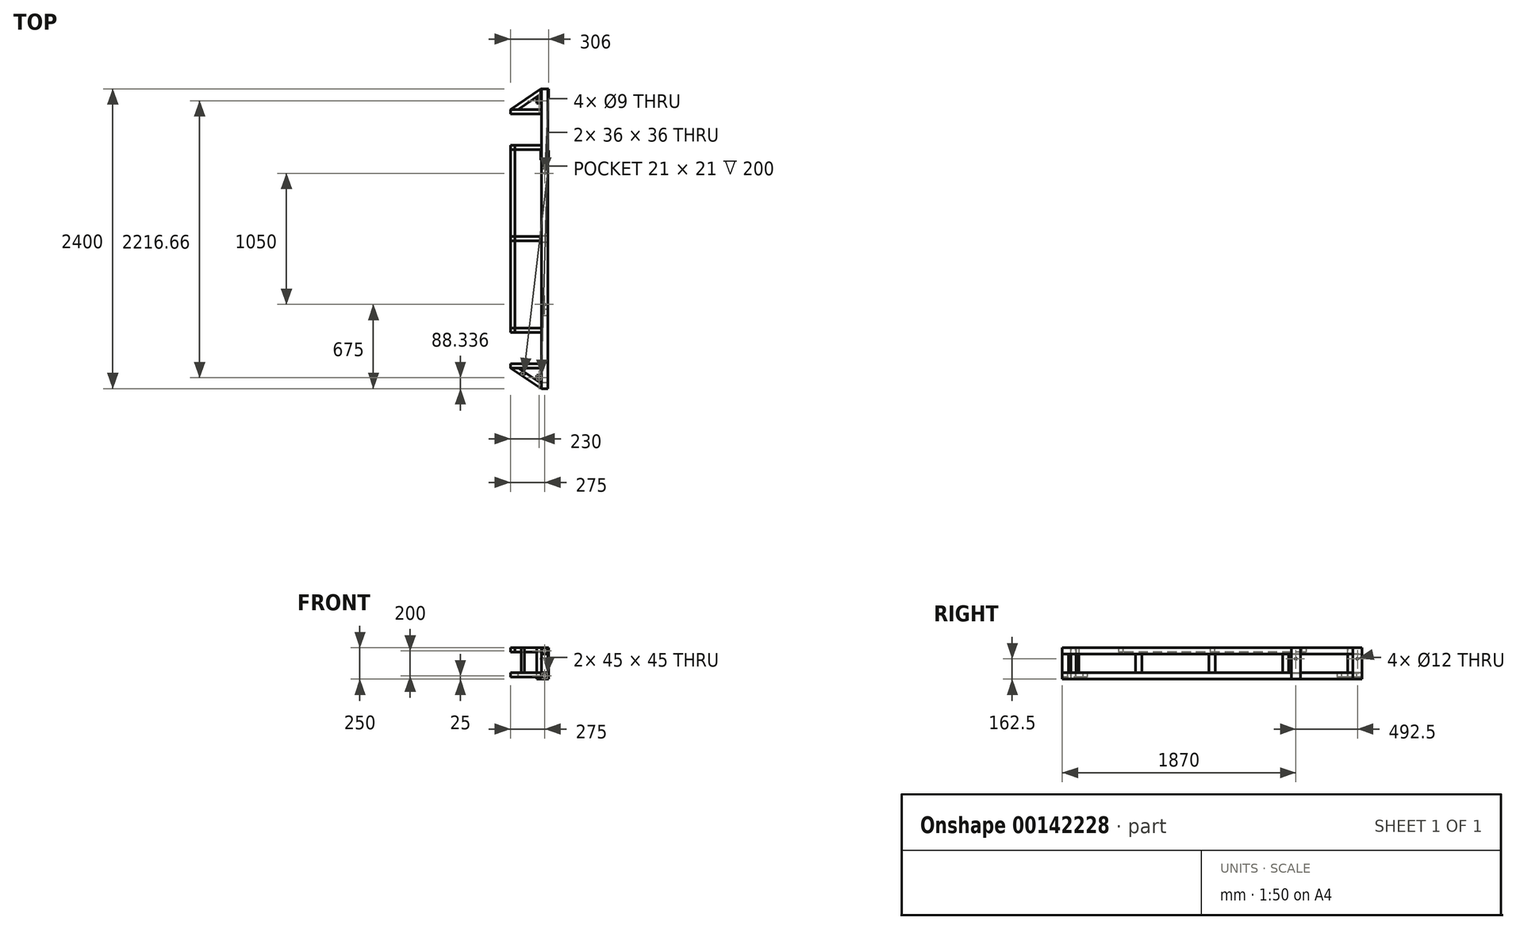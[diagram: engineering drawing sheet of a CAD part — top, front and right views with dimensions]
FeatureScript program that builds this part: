
annotation { "Feature Type Name" : "Feature", "Feature Type Description" : "" }
export const myFeature = defineFeature(function(context is Context, id is Id, definition is map)
    precondition{}
    {
        {
            var Q0;
            Q0=qCreatedBy(makeId("Front.planeOp"),FACE);
            var sketch = newSketch(context, id + "F0", { "sketchPlane" : qUnion([Q0])});
            skLineSegment(sketch, "E0.bottom", {"start": v(0, 125) * mm, "end": v(50, 125) * mm});
            skLineSegment(sketch, "E0.top", {"start": v(0, 75) * mm, "end": v(50, 75) * mm});
            skLineSegment(sketch, "E0.left", {"start": v(0, 125) * mm, "end": v(0, 75) * mm});
            skLineSegment(sketch, "E0.right", {"start": v(50, 125) * mm, "end": v(50, 75) * mm});
            skLineSegment(sketch, "E1.bottom", {"start": v(2.5, 122.5) * mm, "end": v(47.5, 122.5) * mm});
            skLineSegment(sketch, "E1.top", {"start": v(2.5, 77.5) * mm, "end": v(47.5, 77.5) * mm});
            skLineSegment(sketch, "E1.left", {"start": v(2.5, 122.5) * mm, "end": v(2.5, 77.5) * mm});
            skLineSegment(sketch, "E1.right", {"start": v(47.5, 122.5) * mm, "end": v(47.5, 77.5) * mm});
            skLineSegment(sketch, "E2.0.1.0", {"start": v(47.5, -77.5) * mm, "end": v(47.5, -122.5) * mm});
            skLineSegment(sketch, "E2.0.1.1", {"start": v(2.5, -77.5) * mm, "end": v(2.5, -122.5) * mm});
            skLineSegment(sketch, "E2.0.1.2", {"start": v(2.5, -122.5) * mm, "end": v(47.5, -122.5) * mm});
            skLineSegment(sketch, "E2.0.1.3", {"start": v(2.5, -77.5) * mm, "end": v(47.5, -77.5) * mm});
            skLineSegment(sketch, "E2.0.1.4", {"start": v(0, -75) * mm, "end": v(50, -75) * mm});
            skLineSegment(sketch, "E2.0.1.5", {"start": v(50, -75) * mm, "end": v(50, -125) * mm});
            skLineSegment(sketch, "E2.0.1.6", {"start": v(0, -75) * mm, "end": v(0, -125) * mm});
            skLineSegment(sketch, "E2.0.1.7", {"start": v(0, -125) * mm, "end": v(50, -125) * mm});
            skLineSegment(sketch, "E2.direction1", {"start": v(0, 75) * mm, "end": v(25, 75) * mm, "construction": true});
            skLineSegment(sketch, "E2.direction2", {"start": v(0, 75) * mm, "end": v(0, -125) * mm, "construction": true});
            skSolve(sketch);
        }
        {
            var Q0;
            Q0=makeQuery(id+"F0.imprint","IMPRINT",FACE,{"disambiguationData":[TD([[makeQuery(id+"F0.imprint","IMPRINT",EDGE,{"derivedFrom":sQuery(id+"F0.wireOp",EDGE,"E0.bottom")}),-1.0]])]});
            var Q1;
            Q1=makeQuery(id+"F0.imprint","IMPRINT",FACE,{"disambiguationData":[TD([[makeQuery(id+"F0.imprint","IMPRINT",EDGE,{"derivedFrom":sQuery(id+"F0.wireOp",EDGE,"E2.0.1.0")}),1.0]])]});
            extrude(context, id + "F1", {"entities" : qUnion([Q0, Q1]), "endBound" : BoundingType.SYMMETRIC, "depth" : 2400 * mm});
        }
        {
            var Q0;
            Q0=qCreatedBy(makeId("Top.planeOp"),FACE);
            var sketch = newSketch(context, id + "F2", { "sketchPlane" : qUnion([Q0])});
            skLineSegment(sketch, "E3.bottom", {"start": v(0, -1150) * mm, "end": v(50, -1150) * mm});
            skLineSegment(sketch, "E3.top", {"start": v(0, -1200) * mm, "end": v(50, -1200) * mm});
            skLineSegment(sketch, "E3.left", {"start": v(0, -1150) * mm, "end": v(0, -1200) * mm});
            skLineSegment(sketch, "E3.right", {"start": v(50, -1150) * mm, "end": v(50, -1200) * mm});
            skLineSegment(sketch, "E4.0.1.0", {"start": v(0, -562.5) * mm, "end": v(50, -562.5) * mm});
            skLineSegment(sketch, "E4.0.1.1", {"start": v(0, -612.5) * mm, "end": v(50, -612.5) * mm});
            skLineSegment(sketch, "E4.0.1.2", {"start": v(50, -562.5) * mm, "end": v(50, -612.5) * mm});
            skLineSegment(sketch, "E4.0.1.3", {"start": v(0, -562.5) * mm, "end": v(0, -612.5) * mm});
            skLineSegment(sketch, "E4.0.2.0", {"start": v(0, 25) * mm, "end": v(50, 25) * mm});
            skLineSegment(sketch, "E4.0.2.1", {"start": v(0, -25) * mm, "end": v(50, -25) * mm});
            skLineSegment(sketch, "E4.0.2.2", {"start": v(50, 25) * mm, "end": v(50, -25) * mm});
            skLineSegment(sketch, "E4.0.2.3", {"start": v(0, 25) * mm, "end": v(0, -25) * mm});
            skLineSegment(sketch, "E4.0.3.0", {"start": v(0, 612.5) * mm, "end": v(50, 612.5) * mm});
            skLineSegment(sketch, "E4.0.3.1", {"start": v(0, 562.5) * mm, "end": v(50, 562.5) * mm});
            skLineSegment(sketch, "E4.0.3.2", {"start": v(50, 612.5) * mm, "end": v(50, 562.5) * mm});
            skLineSegment(sketch, "E4.0.3.3", {"start": v(0, 612.5) * mm, "end": v(0, 562.5) * mm});
            skLineSegment(sketch, "E4.direction1", {"start": v(0, -1150) * mm, "end": v(25, -1150) * mm, "construction": true});
            skLineSegment(sketch, "E4.direction2", {"start": v(0, -1150) * mm, "end": v(0, -562.5) * mm, "construction": true});
            skLineSegment(sketch, "E5.bottom", {"start": v(50, 1200) * mm, "end": v(56, 1200) * mm});
            skLineSegment(sketch, "E5.top", {"start": v(50, 1125) * mm, "end": v(56, 1125) * mm});
            skLineSegment(sketch, "E5.left", {"start": v(50, 1200) * mm, "end": v(50, 1125) * mm});
            skLineSegment(sketch, "E5.right", {"start": v(56, 1200) * mm, "end": v(56, 1125) * mm});
            skLineSegment(sketch, "E6.0.1.0", {"start": v(50, 707.5) * mm, "end": v(56, 707.5) * mm});
            skLineSegment(sketch, "E6.0.1.1", {"start": v(56, 707.5) * mm, "end": v(56, 632.5) * mm});
            skLineSegment(sketch, "E6.0.1.2", {"start": v(50, 707.5) * mm, "end": v(50, 632.5) * mm});
            skLineSegment(sketch, "E6.0.1.3", {"start": v(50, 632.5) * mm, "end": v(56, 632.5) * mm});
            skLineSegment(sketch, "E6.1.0.0", {"start": v(-6, 1200) * mm, "end": v(0, 1200) * mm});
            skLineSegment(sketch, "E6.1.0.1", {"start": v(0, 1200) * mm, "end": v(0, 1125) * mm});
            skLineSegment(sketch, "E6.1.0.2", {"start": v(-6, 1200) * mm, "end": v(-6, 1125) * mm});
            skLineSegment(sketch, "E6.1.0.3", {"start": v(-6, 1125) * mm, "end": v(0, 1125) * mm});
            skLineSegment(sketch, "E6.1.1.0", {"start": v(-6, 707.5) * mm, "end": v(0, 707.5) * mm});
            skLineSegment(sketch, "E6.1.1.1", {"start": v(0, 707.5) * mm, "end": v(0, 632.5) * mm});
            skLineSegment(sketch, "E6.1.1.2", {"start": v(-6, 707.5) * mm, "end": v(-6, 632.5) * mm});
            skLineSegment(sketch, "E6.1.1.3", {"start": v(-6, 632.5) * mm, "end": v(0, 632.5) * mm});
            skLineSegment(sketch, "E6.direction1", {"start": v(50, 1200) * mm, "end": v(-6, 1200) * mm, "construction": true});
            skLineSegment(sketch, "E6.direction2", {"start": v(50, 1200) * mm, "end": v(50, 707.5) * mm, "construction": true});
            skSolve(sketch);
        }
        {
            var Q0;
            Q0=makeQuery(id+"F2.imprint","IMPRINT",FACE,{"disambiguationData":[TD([[makeQuery(id+"F2.imprint","IMPRINT",EDGE,{"derivedFrom":sQuery(id+"F2.wireOp",EDGE,"E3.bottom")}),-1.0]])]});
            var Q1;
            Q1=makeQuery(id+"F2.imprint","IMPRINT",FACE,{"disambiguationData":[TD([[makeQuery(id+"F2.imprint","IMPRINT",EDGE,{"derivedFrom":sQuery(id+"F2.wireOp",EDGE,"E4.0.1.0")}),-1.0]])]});
            var Q2;
            Q2=makeQuery(id+"F2.imprint","IMPRINT",FACE,{"disambiguationData":[TD([[makeQuery(id+"F2.imprint","IMPRINT",EDGE,{"derivedFrom":sQuery(id+"F2.wireOp",EDGE,"E4.0.2.0")}),-1.0]])]});
            var Q3;
            Q3=makeQuery(id+"F2.imprint","IMPRINT",FACE,{"disambiguationData":[TD([[makeQuery(id+"F2.imprint","IMPRINT",EDGE,{"derivedFrom":sQuery(id+"F2.wireOp",EDGE,"E4.0.3.0")}),-1.0]])]});
            extrude(context, id + "F3", {"entities" : qUnion([Q0, Q1, Q2, Q3]), "endBound" : BoundingType.SYMMETRIC, "depth" : 150 * mm});
        }
        {
            var Q0;
            Q0=makeQuery(id+"F2.imprint","IMPRINT",FACE,{"disambiguationData":[TD([[makeQuery(id+"F2.imprint","IMPRINT",EDGE,{"derivedFrom":sQuery(id+"F2.wireOp",EDGE,"E5.bottom")}),-1.0]])]});
            var Q1;
            Q1=makeQuery(id+"F2.imprint","IMPRINT",FACE,{"disambiguationData":[TD([[makeQuery(id+"F2.imprint","IMPRINT",EDGE,{"derivedFrom":sQuery(id+"F2.wireOp",EDGE,"E6.1.0.0")}),-1.0]])]});
            var Q2;
            Q2=makeQuery(id+"F2.imprint","IMPRINT",FACE,{"disambiguationData":[TD([[makeQuery(id+"F2.imprint","IMPRINT",EDGE,{"derivedFrom":sQuery(id+"F2.wireOp",EDGE,"E6.1.1.0")}),-1.0]])]});
            var Q3;
            Q3=makeQuery(id+"F2.imprint","IMPRINT",FACE,{"disambiguationData":[TD([[makeQuery(id+"F2.imprint","IMPRINT",EDGE,{"derivedFrom":sQuery(id+"F2.wireOp",EDGE,"E6.0.1.0")}),-1.0]])]});
            extrude(context, id + "F4", {"entities" : qUnion([Q0, Q1, Q2, Q3]), "endBound" : BoundingType.SYMMETRIC, "depth" : 250 * mm});
        }
        {
            var Q0;
            Q0=qCreatedBy(makeId("Right.planeOp"),FACE);
            var sketch = newSketch(context, id + "F5", { "sketchPlane" : qUnion([Q0])});
            skLineSegment(sketch, "E7", {"start": v(0, 611.88) * mm, "end": v(0, -633.3) * mm, "construction": true});
            skLineSegment(sketch, "E8.bottom", {"start": v(17.5, 125) * mm, "end": v(-17.5, 125) * mm});
            skLineSegment(sketch, "E8.top", {"start": v(17.5, 90) * mm, "end": v(-17.5, 90) * mm});
            skLineSegment(sketch, "E8.left", {"start": v(17.5, 125) * mm, "end": v(17.5, 90) * mm});
            skLineSegment(sketch, "E8.right", {"start": v(-17.5, 125) * mm, "end": v(-17.5, 90) * mm});
            skLineSegment(sketch, "E9.bottom", {"start": v(-715, 125) * mm, "end": v(-750, 125) * mm});
            skLineSegment(sketch, "E9.top", {"start": v(-715, 90) * mm, "end": v(-750, 90) * mm});
            skLineSegment(sketch, "E9.left", {"start": v(-715, 125) * mm, "end": v(-715, 90) * mm});
            skLineSegment(sketch, "E9.right", {"start": v(-750, 125) * mm, "end": v(-750, 90) * mm});
            skLineSegment(sketch, "E10.bottom", {"start": v(750, 125) * mm, "end": v(715, 125) * mm});
            skLineSegment(sketch, "E10.top", {"start": v(750, 90) * mm, "end": v(715, 90) * mm});
            skLineSegment(sketch, "E10.left", {"start": v(750, 125) * mm, "end": v(750, 90) * mm});
            skLineSegment(sketch, "E10.right", {"start": v(715, 125) * mm, "end": v(715, 90) * mm});
            skLineSegment(sketch, "E11.bottom", {"start": v(1035, -75) * mm, "end": v(1000, -75) * mm});
            skLineSegment(sketch, "E11.top", {"start": v(1035, -110) * mm, "end": v(1000, -110) * mm});
            skLineSegment(sketch, "E11.left", {"start": v(1035, -75) * mm, "end": v(1035, -110) * mm});
            skLineSegment(sketch, "E11.right", {"start": v(1000, -75) * mm, "end": v(1000, -110) * mm});
            skLineSegment(sketch, "E12.bottom", {"start": v(-1000, -75) * mm, "end": v(-1035, -75) * mm});
            skLineSegment(sketch, "E12.top", {"start": v(-1000, -110) * mm, "end": v(-1035, -110) * mm});
            skLineSegment(sketch, "E12.left", {"start": v(-1000, -75) * mm, "end": v(-1000, -110) * mm});
            skLineSegment(sketch, "E12.right", {"start": v(-1035, -75) * mm, "end": v(-1035, -110) * mm});
            skSolve(sketch);
        }
        {
            var Q0;
            Q0=qSketchRegion(id+"F5",true);
            extrude(context, id + "F6", {"entities" : qUnion([Q0]), "oppositeDirection" : true, "depth" : 250 * mm});
        }
        {
            var Q0;
            Q0=makeQuery(id+"F1.opExtrude","SWEPT_FACE",FACE,{"disambiguationData":[OSD([sQuery(id+"F0.wireOp",EDGE,"E2.0.1.4")])]});
            cPlane(context, id + "F7", {"entities" : qUnion([Q0]), "cplaneType" : CPlaneType.OFFSET, "offset" : 0 * mm, "width" : 150 * mm, "height" : 150 * mm});
        }
        {
            var Q0;
            Q0=qCreatedBy(id+"F7.planeOp",FACE);
            var sketch = newSketch(context, id + "F8", { "sketchPlane" : qUnion([Q0])});
            skLineSegment(sketch, "E13", {"start": v(-6, 1200) * mm, "end": v(-249.96, 1035) * mm});
            skLineSegment(sketch, "E14.0", {"start": v(-6, 1157.75) * mm, "end": v(-187.49, 1035) * mm});
            skLineSegment(sketch, "E15", {"start": v(-6, 1200) * mm, "end": v(-6, 1157.75) * mm});
            skLineSegment(sketch, "E16", {"start": v(-249.96, 1035) * mm, "end": v(-187.49, 1035) * mm});
            skLineSegment(sketch, "E17", {"start": v(-250, -1035) * mm, "end": v(0, -1200) * mm});
            skLineSegment(sketch, "E18.0", {"start": v(-186.46, -1035) * mm, "end": v(0, -1158.06) * mm});
            skLineSegment(sketch, "E19", {"start": v(-250, -1035) * mm, "end": v(-186.46, -1035) * mm});
            skLineSegment(sketch, "E20", {"start": v(0, -1158.06) * mm, "end": v(0, -1200) * mm});
            skSolve(sketch);
        }
        {
            var Q0;
            Q0=makeQuery(id+"F8.imprint","IMPRINT",FACE,{"disambiguationData":[TD([[makeQuery(id+"F8.imprint","IMPRINT",EDGE,{"derivedFrom":sQuery(id+"F8.wireOp",EDGE,"E13")}),1.0]])]});
            var Q1;
            Q1=makeQuery(id+"F8.imprint","IMPRINT",FACE,{"disambiguationData":[TD([[makeQuery(id+"F8.imprint","IMPRINT",EDGE,{"derivedFrom":sQuery(id+"F8.wireOp",EDGE,"E17")}),1.0]])]});
            extrude(context, id + "F9", {"entities" : qUnion([Q0, Q1]), "oppositeDirection" : true, "depth" : 35 * mm});
        }
        {
            var Q0;
            Q0=makeQuery(id+"F1.opExtrude","SWEPT_FACE",FACE,{"disambiguationData":[OSD([sQuery(id+"F0.wireOp",EDGE,"E0.bottom")])]});
            cPlane(context, id + "F10", {"entities" : qUnion([Q0]), "cplaneType" : CPlaneType.OFFSET, "offset" : 0 * mm, "width" : 150 * mm, "height" : 150 * mm});
        }
        {
            var Q0;
            Q0=qCreatedBy(id+"F10.planeOp",FACE);
            var sketch = newSketch(context, id + "F11", { "sketchPlane" : qUnion([Q0])});
            skLineSegment(sketch, "E21.bottom", {"start": v(-40, 1125) * mm, "end": v(0, 1125) * mm});
            skLineSegment(sketch, "E21.top", {"start": v(-40, 1085) * mm, "end": v(0, 1085) * mm});
            skLineSegment(sketch, "E21.left", {"start": v(-40, 1125) * mm, "end": v(-40, 1085) * mm});
            skLineSegment(sketch, "E21.right", {"start": v(0, 1125) * mm, "end": v(0, 1085) * mm});
            skLineSegment(sketch, "E22.bottom", {"start": v(-38, 1123) * mm, "end": v(-2, 1123) * mm});
            skLineSegment(sketch, "E22.top", {"start": v(-38, 1087) * mm, "end": v(-2, 1087) * mm});
            skLineSegment(sketch, "E22.left", {"start": v(-38, 1123) * mm, "end": v(-38, 1087) * mm});
            skLineSegment(sketch, "E22.right", {"start": v(-2, 1123) * mm, "end": v(-2, 1087) * mm});
            skLineSegment(sketch, "E23.bottom", {"start": v(-40, -1091.66) * mm, "end": v(0, -1091.66) * mm});
            skLineSegment(sketch, "E23.top", {"start": v(-40, -1131.66) * mm, "end": v(0, -1131.66) * mm});
            skLineSegment(sketch, "E23.left", {"start": v(-40, -1091.66) * mm, "end": v(-40, -1131.66) * mm});
            skLineSegment(sketch, "E23.right", {"start": v(0, -1091.66) * mm, "end": v(0, -1131.66) * mm});
            skLineSegment(sketch, "E24.bottom", {"start": v(-38, -1093.66) * mm, "end": v(-2, -1093.66) * mm});
            skLineSegment(sketch, "E24.top", {"start": v(-38, -1129.66) * mm, "end": v(-2, -1129.66) * mm});
            skLineSegment(sketch, "E24.left", {"start": v(-38, -1093.66) * mm, "end": v(-38, -1129.66) * mm});
            skLineSegment(sketch, "E24.right", {"start": v(-2, -1093.66) * mm, "end": v(-2, -1129.66) * mm});
            skSolve(sketch);
        }
        {
            var Q0;
            Q0=qSketchRegion(id+"F11",true);
            extrude(context, id + "F12", {"entities" : qUnion([Q0]), "oppositeDirection" : true, "depth" : 250 * mm});
        }
        {
            var Q0;
            Q0=makeQuery(id+"F6.opExtrude","CAP_FACE",FACE,{"disambiguationData":[OSD([sQuery(id+"F5.wireOp",EDGE,"E8.bottom"),sQuery(id+"F5.wireOp",EDGE,"E8.top"),sQuery(id+"F5.wireOp",EDGE,"E8.left"),sQuery(id+"F5.wireOp",EDGE,"E8.right")])],"isStart":false});
            cPlane(context, id + "F13", {"entities" : qUnion([Q0]), "cplaneType" : CPlaneType.OFFSET, "offset" : 0 * mm, "width" : 150 * mm, "height" : 150 * mm});
        }
        {
            var Q0;
            Q0=qCreatedBy(id+"F13.planeOp",FACE);
            var sketch = newSketch(context, id + "F14", { "sketchPlane" : qUnion([Q0])});
            skLineSegment(sketch, "E25.bottom", {"start": v(-750, 125) * mm, "end": v(750, 125) * mm});
            skLineSegment(sketch, "E25.top", {"start": v(-750, 90) * mm, "end": v(750, 90) * mm});
            skLineSegment(sketch, "E25.left", {"start": v(-750, 125) * mm, "end": v(-750, 90) * mm});
            skLineSegment(sketch, "E25.right", {"start": v(750, 125) * mm, "end": v(750, 90) * mm});
            skSolve(sketch);
        }
        {
            var Q0;
            Q0=qSketchRegion(id+"F14",true);
            extrude(context, id + "F15", {"entities" : qUnion([Q0]), "oppositeDirection" : true, "depth" : 35 * mm});
        }
        {
            var Q0;
            Q0=qCreatedBy(makeId("Right.planeOp"),FACE);
            var sketch = newSketch(context, id + "F16", { "sketchPlane" : qUnion([Q0])});
            skCircle(sketch, "E26", {"center": v(1162.5, 37.5) * mm, "radius": 6 * mm});
            skCircle(sketch, "E27", {"center": v(670, 37.5) * mm, "radius": 6 * mm});
            skSolve(sketch);
        }
        {
            var Q0;
            Q0=qSketchRegion(id+"F16",true);
            extrude(context, id + "F17", {"entities" : qUnion([Q0]), "operationType" : NewBodyOperationType.REMOVE, "endBound" : BoundingType.SYMMETRIC, "depth" : 200 * mm});
        }
        {
            var Q0;
            Q0=qCreatedBy(makeId("Top.planeOp"),FACE);
            var sketch = newSketch(context, id + "F18", { "sketchPlane" : qUnion([Q0])});
            skCircle(sketch, "E28", {"center": v(25, -525) * mm, "radius": 4.5 * mm});
            skCircle(sketch, "E29", {"center": v(25, 525) * mm, "radius": 4.5 * mm});
            skSolve(sketch);
        }
        {
            var Q0;
            Q0=qSketchRegion(id+"F18",true);
            extrude(context, id + "F19", {"entities" : qUnion([Q0]), "operationType" : NewBodyOperationType.REMOVE, "depth" : 130 * mm});
        }
        {
            var Q0;
            Q0=qCreatedBy(id+"F7.planeOp",FACE);
            var sketch = newSketch(context, id + "F20", { "sketchPlane" : qUnion([Q0])});
            skLineSegment(sketch, "E30.bottom", {"start": v(-162.15, -1068.66) * mm, "end": v(-141.15, -1068.66) * mm});
            skLineSegment(sketch, "E30.top", {"start": v(-162.15, -1089.66) * mm, "end": v(-141.15, -1089.66) * mm});
            skLineSegment(sketch, "E30.left", {"start": v(-162.15, -1068.66) * mm, "end": v(-162.15, -1089.66) * mm});
            skLineSegment(sketch, "E30.right", {"start": v(-141.15, -1068.66) * mm, "end": v(-141.15, -1089.66) * mm});
            skLineSegment(sketch, "E31.bottom", {"start": v(-164.15, -1066.66) * mm, "end": v(-139.15, -1066.66) * mm});
            skLineSegment(sketch, "E31.top", {"start": v(-164.15, -1091.66) * mm, "end": v(-139.15, -1091.66) * mm});
            skLineSegment(sketch, "E31.left", {"start": v(-164.15, -1066.66) * mm, "end": v(-164.15, -1091.66) * mm});
            skLineSegment(sketch, "E31.right", {"start": v(-139.15, -1066.66) * mm, "end": v(-139.15, -1091.66) * mm});
            skSolve(sketch);
        }
        {
            var Q0;
            Q0=qSketchRegion(id+"F20",true);
            extrude(context, id + "F21", {"entities" : qUnion([Q0]), "operationType" : NewBodyOperationType.ADD, "depth" : 200 * mm});
        }
    });
